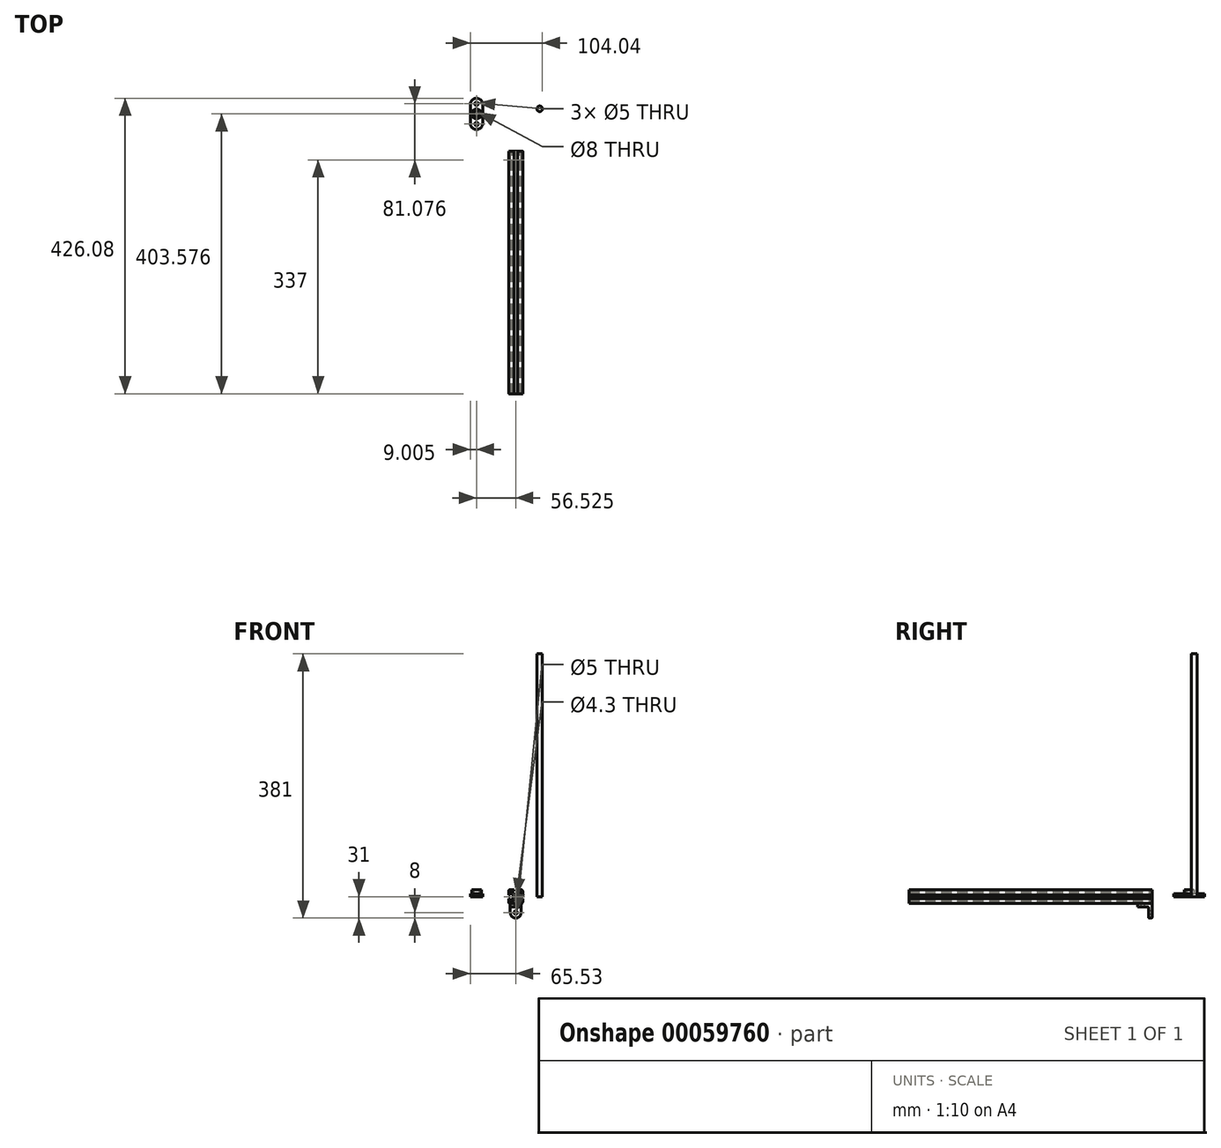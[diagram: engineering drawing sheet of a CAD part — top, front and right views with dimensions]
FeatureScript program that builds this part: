
annotation { "Feature Type Name" : "Feature", "Feature Type Description" : "" }
export const myFeature = defineFeature(function(context is Context, id is Id, definition is map)
    precondition{}
    {
        {
            var Q0;
            Q0=qCreatedBy(makeId("Front.planeOp"),FACE);
            var sketch = newSketch(context, id + "F0", { "sketchPlane" : qUnion([Q0])});
            skCircle(sketch, "E0", {"center": v(0, 0) * mm, "radius": 2.15 * mm});
            skLineSegment(sketch, "E1.bottom", {"start": v(-8, 10) * mm, "end": v(-2.5, 10) * mm});
            skLineSegment(sketch, "E1.top", {"start": v(-8, -10) * mm, "end": v(-2.5, -10) * mm});
            skLineSegment(sketch, "E1.left", {"start": v(-10, 8) * mm, "end": v(-10, 2.5) * mm});
            skLineSegment(sketch, "E1.right", {"start": v(10, 8) * mm, "end": v(10, 2.5) * mm});
            skLineSegment(sketch, "E2", {"start": v(-2.5, -19.05) * mm, "end": v(-2.5, -8.2) * mm, "construction": true});
            skLineSegment(sketch, "E3", {"start": v(-19.35, 2.5) * mm, "end": v(-8.2, 2.5) * mm, "construction": true});
            skLineSegment(sketch, "E4.MirrorCS", {"start": v(-19.35, -2.5) * mm, "end": v(-8.2, -2.5) * mm, "construction": true});
            skLineSegment(sketch, "E5.MirrorCS", {"start": v(2.5, -19.05) * mm, "end": v(2.5, -8.2) * mm, "construction": true});
            skPoint(sketch, "E6.visualSharp", {"position": v(-10, 10) * mm});
            skArc(sketch, "E6.filletArc", {"start": v(-8, 10) * mm, "mid": v(-9.41, 9.41) * mm, "end": v(-10, 8) * mm});
            skPoint(sketch, "E7.visualSharp", {"position": v(-10, -10) * mm});
            skArc(sketch, "E7.filletArc", {"start": v(-10, -8) * mm, "mid": v(-9.41, -9.41) * mm, "end": v(-8, -10) * mm});
            skPoint(sketch, "E8.visualSharp", {"position": v(10, 10) * mm});
            skArc(sketch, "E8.filletArc", {"start": v(10, 8) * mm, "mid": v(9.41, 9.41) * mm, "end": v(8, 10) * mm});
            skPoint(sketch, "E9.visualSharp", {"position": v(10, -10) * mm});
            skArc(sketch, "E9.filletArc", {"start": v(8, -10) * mm, "mid": v(9.41, -9.41) * mm, "end": v(10, -8) * mm});
            skLineSegment(sketch, "E10.bottom", {"start": v(-5.72, 8.2) * mm, "end": v(-2.5, 8.2) * mm, "construction": true});
            skLineSegment(sketch, "E10.top", {"start": v(-5.72, -8.2) * mm, "end": v(-2.5, -8.2) * mm});
            skLineSegment(sketch, "E10.left", {"start": v(-8.2, 5.84) * mm, "end": v(-8.2, 2.5) * mm});
            skLineSegment(sketch, "E10.right", {"start": v(8.2, 5.72) * mm, "end": v(8.2, 2.5) * mm});
            skLineSegment(sketch, "E11", {"start": v(-2.5, -8.2) * mm, "end": v(-2.5, -10) * mm});
            skLineSegment(sketch, "E12", {"start": v(2.5, -8.2) * mm, "end": v(2.5, -10) * mm});
            skLineSegment(sketch, "E13", {"start": v(-8.2, -2.5) * mm, "end": v(-10, -2.5) * mm});
            skLineSegment(sketch, "E14", {"start": v(-8.2, 2.5) * mm, "end": v(-10, 2.5) * mm});
            skLineSegment(sketch, "E15", {"start": v(8.2, 2.5) * mm, "end": v(10, 2.5) * mm});
            skLineSegment(sketch, "E16", {"start": v(-2.5, 8.2) * mm, "end": v(-2.5, 10) * mm});
            skLineSegment(sketch, "E17", {"start": v(2.5, 8.2) * mm, "end": v(2.5, 10) * mm});
            skLineSegment(sketch, "E18", {"start": v(-9.41, -9.41) * mm, "end": v(-1.52, -1.52) * mm, "construction": true});
            skLineSegment(sketch, "E19", {"start": v(-9.41, 9.41) * mm, "end": v(-2.5, 2.5) * mm, "construction": true});
            skLineSegment(sketch, "E20", {"start": v(-7.35, -6.07) * mm, "end": v(-3.65, -2.38) * mm});
            skLineSegment(sketch, "E21.MirrorCS", {"start": v(-6.07, -7.35) * mm, "end": v(-2.38, -3.65) * mm});
            skPoint(sketch, "E22.orphan", {"position": v(-11.42, 10.14) * mm});
            skPoint(sketch, "E23.orphan", {"position": v(-10.14, 11.42) * mm});
            skPoint(sketch, "E24.orphan", {"position": v(10.4, 11.68) * mm});
            skPoint(sketch, "E25.orphan", {"position": v(11.68, 10.4) * mm});
            skPoint(sketch, "E26.orphan", {"position": v(11.6, -10.32) * mm});
            skPoint(sketch, "E27.orphan", {"position": v(10.32, -11.6) * mm});
            skPoint(sketch, "E28.orphan", {"position": v(-13.16, -14.44) * mm});
            skPoint(sketch, "E29.orphan", {"position": v(-14.44, -13.16) * mm});
            skLineSegment(sketch, "E30.bottom", {"start": v(-2.38, 3.65) * mm, "end": v(2.38, 3.65) * mm});
            skLineSegment(sketch, "E30.top", {"start": v(-2.38, -3.65) * mm, "end": v(2.38, -3.65) * mm});
            skLineSegment(sketch, "E30.left", {"start": v(-3.65, 2.5) * mm, "end": v(-3.65, -2.38) * mm});
            skLineSegment(sketch, "E30.right", {"start": v(3.65, 2.38) * mm, "end": v(3.65, -2.38) * mm});
            skLineSegment(sketch, "E31.trimOffspring", {"start": v(2.38, -3.65) * mm, "end": v(6.07, -7.35) * mm});
            skLineSegment(sketch, "E32.trimOffspring", {"start": v(1.52, -1.52) * mm, "end": v(9.41, -9.41) * mm, "construction": true});
            skLineSegment(sketch, "E33.trimOffspring", {"start": v(3.65, -2.38) * mm, "end": v(7.35, -6.07) * mm});
            skLineSegment(sketch, "E34.trimOffspring", {"start": v(0, 0) * mm, "end": v(1.72, 1.72) * mm, "construction": true});
            skLineSegment(sketch, "E35.trimOffspring", {"start": v(1.52, 1.52) * mm, "end": v(9.41, 9.41) * mm, "construction": true});
            skLineSegment(sketch, "E36.trimOffspring", {"start": v(3.65, 2.38) * mm, "end": v(7.35, 6.07) * mm});
            skLineSegment(sketch, "E37.trimOffspring", {"start": v(8.2, 2.5) * mm, "end": v(18.34, 2.5) * mm, "construction": true});
            skLineSegment(sketch, "E38.trimOffspring", {"start": v(8.2, -2.5) * mm, "end": v(18.34, -2.5) * mm, "construction": true});
            skLineSegment(sketch, "E39.trimOffspring", {"start": v(-3.65, 2.5) * mm, "end": v(1.23, 2.5) * mm, "construction": true});
            skLineSegment(sketch, "E40.trimOffspring", {"start": v(-2.5, 8.2) * mm, "end": v(-2.5, 13.53) * mm, "construction": true});
            skLineSegment(sketch, "E41.trimOffspring", {"start": v(2.5, 8.2) * mm, "end": v(2.5, 13.53) * mm, "construction": true});
            skLineSegment(sketch, "E42", {"start": v(2.5, 8.2) * mm, "end": v(6.93, 8.2) * mm});
            skLineSegment(sketch, "E43", {"start": v(6.93, 8.2) * mm, "end": v(2.38, 3.65) * mm});
            skLineSegment(sketch, "E44", {"start": v(2.38, 3.65) * mm, "end": v(-2.38, 3.65) * mm});
            skLineSegment(sketch, "E45", {"start": v(-6.93, 8.2) * mm, "end": v(-2.5, 8.2) * mm});
            skLineSegment(sketch, "E46", {"start": v(-6.07, 7.35) * mm, "end": v(-2.38, 3.65) * mm});
            skLineSegment(sketch, "E47.trimOffspring", {"start": v(2.5, 8.2) * mm, "end": v(5.72, 8.2) * mm, "construction": true});
            skLineSegment(sketch, "E48.trimOffspring", {"start": v(8.2, -2.5) * mm, "end": v(8.2, -5.72) * mm});
            skLineSegment(sketch, "E49.trimOffspring", {"start": v(2.5, -8.2) * mm, "end": v(5.72, -8.2) * mm});
            skLineSegment(sketch, "E50.trimOffspring", {"start": v(-8.2, -2.5) * mm, "end": v(-8.2, -5.72) * mm});
            skPoint(sketch, "E51.orphan", {"position": v(3.65, 3.65) * mm});
            skPoint(sketch, "E52.orphan", {"position": v(3.65, -3.65) * mm});
            skPoint(sketch, "E53.orphan", {"position": v(-3.65, -3.65) * mm});
            skPoint(sketch, "E54.orphan", {"position": v(-3.65, 3.65) * mm});
            skLineSegment(sketch, "E55.trimOffspring", {"start": v(2.38, 3.65) * mm, "end": v(6.07, 7.35) * mm, "construction": true});
            skPoint(sketch, "E56.orphan", {"position": v(-8.2, 8.2) * mm});
            skPoint(sketch, "E57.orphan", {"position": v(8.2, 8.2) * mm});
            skPoint(sketch, "E58.orphan", {"position": v(8.2, -8.2) * mm});
            skPoint(sketch, "E59.orphan", {"position": v(-8.2, -8.2) * mm});
            skLineSegment(sketch, "E60.trimOffspring", {"start": v(2.5, 10) * mm, "end": v(8, 10) * mm});
            skLineSegment(sketch, "E61.trimOffspring", {"start": v(-10, -2.5) * mm, "end": v(-10, -8) * mm});
            skLineSegment(sketch, "E62.trimOffspring", {"start": v(2.5, -10) * mm, "end": v(8, -10) * mm});
            skLineSegment(sketch, "E63.trimOffspring", {"start": v(10, -2.5) * mm, "end": v(10, -8) * mm});
            skLineSegment(sketch, "E64", {"start": v(-7.35, 6.2) * mm, "end": v(-3.65, 2.5) * mm});
            skPoint(sketch, "E65.visualSharp", {"position": v(-8.2, 7.05) * mm});
            skArc(sketch, "E65.filletArc", {"start": v(-7.35, 6.2) * mm, "mid": v(-7.9, 6.3) * mm, "end": v(-8.2, 5.84) * mm});
            skPoint(sketch, "E66.visualSharp", {"position": v(-6.93, 8.2) * mm});
            skArc(sketch, "E66.filletArc", {"start": v(-5.72, 8.2) * mm, "mid": v(-6.18, 7.9) * mm, "end": v(-6.07, 7.35) * mm});
            skPoint(sketch, "E67.visualSharp", {"position": v(6.93, 8.2) * mm});
            skArc(sketch, "E67.filletArc", {"start": v(6.07, 7.35) * mm, "mid": v(6.18, 7.9) * mm, "end": v(5.72, 8.2) * mm, "construction": true});
            skPoint(sketch, "E68.visualSharp", {"position": v(8.2, 6.93) * mm});
            skArc(sketch, "E68.filletArc", {"start": v(8.2, 5.72) * mm, "mid": v(7.9, 6.18) * mm, "end": v(7.35, 6.07) * mm});
            skPoint(sketch, "E69.visualSharp", {"position": v(8.2, -6.93) * mm});
            skArc(sketch, "E69.filletArc", {"start": v(7.35, -6.07) * mm, "mid": v(7.9, -6.18) * mm, "end": v(8.2, -5.72) * mm});
            skPoint(sketch, "E70.visualSharp", {"position": v(6.93, -8.2) * mm});
            skArc(sketch, "E70.filletArc", {"start": v(5.72, -8.2) * mm, "mid": v(6.18, -7.9) * mm, "end": v(6.07, -7.35) * mm});
            skPoint(sketch, "E71.visualSharp", {"position": v(-6.93, -8.2) * mm});
            skArc(sketch, "E71.filletArc", {"start": v(-6.07, -7.35) * mm, "mid": v(-6.18, -7.9) * mm, "end": v(-5.72, -8.2) * mm});
            skPoint(sketch, "E72.visualSharp", {"position": v(-8.2, -6.93) * mm});
            skArc(sketch, "E72.filletArc", {"start": v(-8.2, -5.72) * mm, "mid": v(-7.9, -6.18) * mm, "end": v(-7.35, -6.07) * mm});
            skLineSegment(sketch, "E73", {"start": v(8.2, -2.5) * mm, "end": v(10, -2.5) * mm});
            skLineSegment(sketch, "E74", {"start": v(-5.21, 4.06) * mm, "end": v(-5.21, -3.94) * mm});
            skSolve(sketch);
        }
        {
            var Q0;
            Q0=makeQuery(id+"F0.imprint","IMPRINT",FACE,{"disambiguationData":[TD([[makeQuery(id+"F0.imprint","IMPRINT",EDGE,{"derivedFrom":sQuery(id+"F0.wireOp",EDGE,"E0")}),-1.0]])]});
            extrude(context, id + "F1", {"entities" : qUnion([Q0]), "depth" : 350 * mm});
        }
        {
            var Q0;
            Q0=makeQuery(id+"F1.opExtrude","SWEPT_FACE",FACE,{"disambiguationData":[OSD([sQuery(id+"F0.wireOp",EDGE,"E1.top")])]});
            var sketch = newSketch(context, id + "F2", { "sketchPlane" : qUnion([Q0])});
            skLineSegment(sketch, "E75.bottom", {"start": v(-7.8, 0) * mm, "end": v(7.8, 0) * mm});
            skLineSegment(sketch, "E75.top", {"start": v(-7.8, 21) * mm, "end": v(7.8, 21) * mm});
            skLineSegment(sketch, "E75.left", {"start": v(-7.8, 0) * mm, "end": v(-7.8, 21) * mm});
            skLineSegment(sketch, "E75.right", {"start": v(7.8, 0) * mm, "end": v(7.8, 21) * mm});
            skCircle(sketch, "E76", {"center": v(0, 13) * mm, "radius": 2.5 * mm});
            skPoint(sketch, "E76.centerSnap0", {"position": v(0, 21) * mm});
            skLineSegment(sketch, "E77.bottom", {"start": v(-4.8, 21) * mm, "end": v(4.8, 21) * mm});
            skLineSegment(sketch, "E77.top", {"start": v(-4.8, 5) * mm, "end": v(4.8, 5) * mm});
            skLineSegment(sketch, "E77.left", {"start": v(-4.8, 21) * mm, "end": v(-4.8, 5) * mm});
            skLineSegment(sketch, "E77.right", {"start": v(4.8, 21) * mm, "end": v(4.8, 5) * mm});
            skSolve(sketch);
        }
        {
            var Q0;
            Q0 = qSketchRegion(id + "F2", true);
            var Q1;
            Q1=makeQuery(id+"F2.imprint","IMPRINT",FACE,{"disambiguationData":[TD([[makeQuery(id+"F2.imprint","IMPRINT",EDGE,{"derivedFrom":sQuery(id+"F2.wireOp",EDGE,"E76")}),1.0]])]});
            extrude(context, id + "F3", {"entities" : qUnion([Q0, Q1]), "depth" : 21 * mm});
        }
        {
            var Q0;
            {var subQ4=sQuery(id+"F2.wireOp",EDGE,"E77.left");Q0=makeQuery(id+"F2.imprint","IMPRINT",FACE,{"disambiguationData":[TD([[makeQuery(id+"F2.imprint","IMPRINT",EDGE,{"derivedFrom":subQ4}),1.0]])]});}
            var Q1;
            {var subQ6=sQuery(id+"F2.wireOp",EDGE,"E76");Q1=makeQuery(id+"F2.imprint","IMPRINT",FACE,{"disambiguationData":[TD([[makeQuery(id+"F2.imprint","IMPRINT",EDGE,{"derivedFrom":subQ6}),-1.0]])]});}
            var Q2;
            Q2=makeQuery(id+"F2.imprint","IMPRINT",FACE,{"disambiguationData":[TD([[makeQuery(id+"F2.imprint","IMPRINT",EDGE,{"derivedFrom":sQuery(id+"F2.wireOp",EDGE,"E76")}),1.0]])]});
            extrude(context, id + "F4", {"entities" : qUnion([Q0, Q1, Q2]), "operationType" : NewBodyOperationType.REMOVE, "endBound" : BoundingType.THROUGH_ALL, "depth" : 3 * mm, "hasSecondDirection" : true, "secondDirectionOppositeDirection" : false, "secondDirectionDepth" : 5 * mm});
        }
        {
            var Q0;
            Q0=makeQuery(id+"F2.imprint","IMPRINT",FACE,{"disambiguationData":[TD([[makeQuery(id+"F2.imprint","IMPRINT",EDGE,{"derivedFrom":sQuery(id+"F2.wireOp",EDGE,"E76")}),1.0]])]});
            extrude(context, id + "F5", {"entities" : qUnion([Q0]), "operationType" : NewBodyOperationType.REMOVE, "endBound" : BoundingType.THROUGH_ALL, "depth" : 25 * mm});
        }
        {
            var Q0;
            Q0=makeQuery(id+"F4.boolean.opBoolean","COPY",FACE,{"derivedFrom":makeQuery(id+"F4.opExtrude","SWEPT_FACE",FACE,{"disambiguationData":[OSD([sQuery(id+"F2.wireOp",EDGE,"E77.top")])]})});
            var sketch = newSketch(context, id + "F6", { "sketchPlane" : qUnion([Q0])});
            skLineSegment(sketch, "E78.0.0", {"start": v(4.8, -31) * mm, "end": v(4.8, -15) * mm});
            skLineSegment(sketch, "E78.0.1", {"start": v(4.8, -15) * mm, "end": v(-4.8, -15) * mm});
            skLineSegment(sketch, "E78.0.2", {"start": v(-4.8, -15) * mm, "end": v(-4.8, -31) * mm});
            skLineSegment(sketch, "E78.0.3", {"start": v(-4.8, -31) * mm, "end": v(4.8, -31) * mm});
            skPoint(sketch, "E79.centerSnap0", {"position": v(-4.8, -23) * mm});
            skCircle(sketch, "E80", {"center": v(0, -23) * mm, "radius": 2.5 * mm});
            skSolve(sketch);
        }
        {
            var Q0;
            Q0=makeQuery(id+"F6.imprint","IMPRINT",FACE,{"disambiguationData":[TD([[makeQuery(id+"F6.imprint","IMPRINT",EDGE,{"derivedFrom":sQuery(id+"F6.wireOp",EDGE,"E79")}),1.0]])]});
            var Q1;
            Q1=makeQuery(id+"F6.imprint","IMPRINT",FACE,{"disambiguationData":[TD([[makeQuery(id+"F6.imprint","IMPRINT",EDGE,{"derivedFrom":sQuery(id+"F6.wireOp",EDGE,"E80")}),1.0]])]});
            extrude(context, id + "F7", {"entities" : qUnion([Q0, Q1]), "operationType" : NewBodyOperationType.REMOVE, "endBound" : BoundingType.THROUGH_ALL, "oppositeDirection" : true, "depth" : 25 * mm});
        }
        {
            var Q0;
            Q0=makeQuery(id+"F3.opExtrude","SWEPT_FACE",FACE,{"disambiguationData":[OSD([sQuery(id+"F2.wireOp",EDGE,"E75.right")])]});
            var sketch = newSketch(context, id + "F8", { "sketchPlane" : qUnion([Q0])});
            skLineSegment(sketch, "E81.0", {"start": v(-5, -31) * mm, "end": v(-5, -15) * mm});
            skLineSegment(sketch, "E82.0", {"start": v(-21, -15) * mm, "end": v(-5, -15) * mm});
            skSolve(sketch);
        }
        {
            var Q0;
            Q0=makeQuery(id+"F8.imprint","IMPRINT",FACE,{"disambiguationData":[TD([[makeQuery(id+"F8.imprint","IMPRINT",EDGE,{"derivedFrom":sQuery(id+"F8.wireOp",EDGE,"E81.0")}),1.0]])]});
            extrude(context, id + "F9", {"entities" : qUnion([Q0]), "operationType" : NewBodyOperationType.REMOVE, "oppositeDirection" : true, "depth" : 25 * mm});
        }
        {
            var Q0;
            Q0=makeQuery(id+"F3.opExtrude","SWEPT_EDGE",EDGE,{"disambiguationData":[OSD([sQuery(id+"F2.wireOp",EDGE,"E75.top"),sQuery(id+"F2.wireOp",EDGE,"E75.left")])]});
            var Q1;
            Q1=makeQuery(id+"F3.opExtrude","SWEPT_EDGE",EDGE,{"disambiguationData":[OSD([sQuery(id+"F2.wireOp",EDGE,"E75.top"),sQuery(id+"F2.wireOp",EDGE,"E75.right")])]});
            var Q2;
            Q2=makeQuery(id+"F3.opExtrude","CAP_EDGE",EDGE,{"disambiguationData":[OSD([sQuery(id+"F2.wireOp",EDGE,"E75.left")])],"isStart":false});
            var Q3;
            Q3=makeQuery(id+"F3.opExtrude","CAP_EDGE",EDGE,{"disambiguationData":[OSD([sQuery(id+"F2.wireOp",EDGE,"E75.right")])],"isStart":false});
            fillet(context, id + "F10", {"entities" : qUnion([Q0, Q1, Q2, Q3]), "radius" : 8 * mm, "tangentPropagation" : true, "allowEdgeOverflow" : false});
        }
        {
            var Q0;
            Q0=makeQuery(id+"F3.opExtrude","CAP_EDGE",EDGE,{"disambiguationData":[OSD([sQuery(id+"F2.wireOp",EDGE,"E75.bottom")])],"isStart":true});
            var Q1;
            Q1=makeQuery(id+"F4.boolean.opBoolean","COPY",EDGE,{"derivedFrom":makeQuery(id+"F4.opExtrude","CAP_EDGE",EDGE,{"disambiguationData":[OSD([sQuery(id+"F2.wireOp",EDGE,"E77.top")])],"isStart":true})});
            var Q2;
            Q2=makeQuery(id+"F3.opExtrude","SWEPT_EDGE",EDGE,{"disambiguationData":[OSD([sQuery(id+"F0.wireOp",EDGE,"E1.top"),sQuery(id+"F2.wireOp",EDGE,"E75.bottom"),sQuery(id+"F2.wireOp",EDGE,"E75.left")])]});
            var Q3;
            Q3=makeQuery(id+"F10.opFillet","BLEND_EDGE",EDGE,{"blendedFrom":[makeQuery(id+"F3.opExtrude","CAP_EDGE",EDGE,{"disambiguationData":[OSD([sQuery(id+"F2.wireOp",EDGE,"E75.left")])],"isStart":false}),makeQuery(id+"F3.opExtrude","SWEPT_FACE",FACE,{"disambiguationData":[OSD([sQuery(id+"F2.wireOp",EDGE,"E75.bottom")])]})],"blendedInto":[makeQuery(id+"F3.opExtrude","SWEPT_FACE",FACE,{"disambiguationData":[OSD([sQuery(id+"F2.wireOp",EDGE,"E75.bottom")])]})]});
            var Q4;
            Q4=makeQuery(id+"F10.opFillet","BLEND_EDGE",EDGE,{"blendedFrom":[makeQuery(id+"F3.opExtrude","CAP_EDGE",EDGE,{"disambiguationData":[OSD([sQuery(id+"F2.wireOp",EDGE,"E75.right")])],"isStart":false}),makeQuery(id+"F3.opExtrude","SWEPT_FACE",FACE,{"disambiguationData":[OSD([sQuery(id+"F2.wireOp",EDGE,"E75.bottom")])]})],"blendedInto":[makeQuery(id+"F3.opExtrude","SWEPT_FACE",FACE,{"disambiguationData":[OSD([sQuery(id+"F2.wireOp",EDGE,"E75.bottom")])]})]});
            var Q5;
            Q5=makeQuery(id+"F3.opExtrude","SWEPT_EDGE",EDGE,{"disambiguationData":[OSD([sQuery(id+"F2.wireOp",EDGE,"E75.bottom"),sQuery(id+"F2.wireOp",EDGE,"E75.right")])]});
            var Q6;
            Q6=makeQuery(id+"F3.opExtrude","CAP_EDGE",EDGE,{"disambiguationData":[OSD([sQuery(id+"F2.wireOp",EDGE,"E75.left")])],"isStart":true});
            var Q7;
            {var subQ0=sQuery(id+"F2.wireOp",EDGE,"E75.left");var subQ1=sQuery(id+"F2.wireOp",EDGE,"E75.top");Q7=makeQuery(id+"F10.opFillet","BLEND_EDGE",EDGE,{"blendedFrom":[makeQuery(id+"F3.opExtrude","SWEPT_EDGE",EDGE,{"disambiguationData":[OSD([subQ1,subQ0])]}),makeQuery(id+"F3.opExtrude","CAP_FACE",FACE,{"disambiguationData":[OSD([sQuery(id+"F2.wireOp",EDGE,"E75.bottom"),subQ1,subQ0,sQuery(id+"F2.wireOp",EDGE,"E75.right"),sQuery(id+"F2.wireOp",EDGE,"E77.bottom"),sQuery(id+"F2.wireOp",EDGE,"m4iLFzGu-l6cL-oS4W-GvPt-0jt0GClDsFra")])],"isStart":true})],"blendedInto":[makeQuery(id+"F3.opExtrude","CAP_FACE",FACE,{"disambiguationData":[OSD([sQuery(id+"F2.wireOp",EDGE,"E75.bottom"),subQ1,subQ0,sQuery(id+"F2.wireOp",EDGE,"E75.right"),sQuery(id+"F2.wireOp",EDGE,"E77.bottom"),sQuery(id+"F2.wireOp",EDGE,"m4iLFzGu-l6cL-oS4W-GvPt-0jt0GClDsFra")])],"isStart":true})]});}
            var Q8;
            {var subQ0=sQuery(id+"F2.wireOp",EDGE,"E75.right");var subQ1=sQuery(id+"F2.wireOp",EDGE,"E75.top");Q8=makeQuery(id+"F10.opFillet","BLEND_EDGE",EDGE,{"blendedFrom":[makeQuery(id+"F3.opExtrude","SWEPT_EDGE",EDGE,{"disambiguationData":[OSD([subQ1,subQ0])]}),makeQuery(id+"F3.opExtrude","CAP_FACE",FACE,{"disambiguationData":[OSD([sQuery(id+"F2.wireOp",EDGE,"E75.bottom"),subQ1,sQuery(id+"F2.wireOp",EDGE,"E75.left"),subQ0,sQuery(id+"F2.wireOp",EDGE,"E77.bottom"),sQuery(id+"F2.wireOp",EDGE,"m4iLFzGu-l6cL-oS4W-GvPt-0jt0GClDsFra")])],"isStart":true})],"blendedInto":[makeQuery(id+"F3.opExtrude","CAP_FACE",FACE,{"disambiguationData":[OSD([sQuery(id+"F2.wireOp",EDGE,"E75.bottom"),subQ1,sQuery(id+"F2.wireOp",EDGE,"E75.left"),subQ0,sQuery(id+"F2.wireOp",EDGE,"E77.bottom"),sQuery(id+"F2.wireOp",EDGE,"m4iLFzGu-l6cL-oS4W-GvPt-0jt0GClDsFra")])],"isStart":true})]});}
            var Q9;
            Q9=makeQuery(id+"F3.opExtrude","CAP_EDGE",EDGE,{"disambiguationData":[OSD([sQuery(id+"F2.wireOp",EDGE,"E75.right")])],"isStart":true});
            var Q10;
            Q10=makeQuery(id+"F9.boolean.opBoolean","INTERSECT",EDGE,{"derivedFrom":[makeQuery(id+"F3.opExtrude","SWEPT_FACE",FACE,{"disambiguationData":[OSD([sQuery(id+"F2.wireOp",EDGE,"E75.left")])]}),makeQuery(id+"F9.opExtrude","SWEPT_FACE",FACE,{"disambiguationData":[OSD([sQuery(id+"F8.wireOp",EDGE,"E81.0")])]})]});
            var Q11;
            Q11=makeQuery(id+"F10.opFillet","BLEND_EDGE",EDGE,{"blendedFrom":[makeQuery(id+"F3.opExtrude","CAP_EDGE",EDGE,{"disambiguationData":[OSD([sQuery(id+"F2.wireOp",EDGE,"E75.left")])],"isStart":false}),makeQuery(id+"F9.boolean.opBoolean","MERGE",FACE,{"derivedFrom":[makeQuery(id+"F4.boolean.opBoolean","COPY",FACE,{"derivedFrom":makeQuery(id+"F4.opExtrude","SWEPT_FACE",FACE,{"disambiguationData":[OSD([sQuery(id+"F2.wireOp",EDGE,"E77.top")])]})}),makeQuery(id+"F9.opExtrude","SWEPT_FACE",FACE,{"disambiguationData":[OSD([sQuery(id+"F8.wireOp",EDGE,"E81.0")])]})]})],"blendedInto":[makeQuery(id+"F9.boolean.opBoolean","MERGE",FACE,{"derivedFrom":[makeQuery(id+"F4.boolean.opBoolean","COPY",FACE,{"derivedFrom":makeQuery(id+"F4.opExtrude","SWEPT_FACE",FACE,{"disambiguationData":[OSD([sQuery(id+"F2.wireOp",EDGE,"E77.top")])]})}),makeQuery(id+"F9.opExtrude","SWEPT_FACE",FACE,{"disambiguationData":[OSD([sQuery(id+"F8.wireOp",EDGE,"E81.0")])]})]})]});
            var Q12;
            Q12=makeQuery(id+"F10.opFillet","BLEND_EDGE",EDGE,{"blendedFrom":[makeQuery(id+"F3.opExtrude","CAP_EDGE",EDGE,{"disambiguationData":[OSD([sQuery(id+"F2.wireOp",EDGE,"E75.right")])],"isStart":false}),makeQuery(id+"F9.boolean.opBoolean","MERGE",FACE,{"derivedFrom":[makeQuery(id+"F4.boolean.opBoolean","COPY",FACE,{"derivedFrom":makeQuery(id+"F4.opExtrude","SWEPT_FACE",FACE,{"disambiguationData":[OSD([sQuery(id+"F2.wireOp",EDGE,"E77.top")])]})}),makeQuery(id+"F9.opExtrude","SWEPT_FACE",FACE,{"disambiguationData":[OSD([sQuery(id+"F8.wireOp",EDGE,"E81.0")])]})]})],"blendedInto":[makeQuery(id+"F9.boolean.opBoolean","MERGE",FACE,{"derivedFrom":[makeQuery(id+"F4.boolean.opBoolean","COPY",FACE,{"derivedFrom":makeQuery(id+"F4.opExtrude","SWEPT_FACE",FACE,{"disambiguationData":[OSD([sQuery(id+"F2.wireOp",EDGE,"E77.top")])]})}),makeQuery(id+"F9.opExtrude","SWEPT_FACE",FACE,{"disambiguationData":[OSD([sQuery(id+"F8.wireOp",EDGE,"E81.0")])]})]})]});
            fillet(context, id + "F11", {"entities" : qUnion([Q0, Q1, Q2, Q3, Q4, Q5, Q6, Q7, Q8, Q9, Q10, Q11, Q12]), "radius" : 1 * mm, "tangentPropagation" : true, "allowEdgeOverflow" : false});
        }
        {
            var Q0;
            Q0=qCreatedBy(makeId("Top.planeOp"),FACE);
            var sketch = newSketch(context, id + "F12", { "sketchPlane" : qUnion([Q0])});
            skCircle(sketch, "E83", {"center": v(34.51, 60.98) * mm, "radius": 4 * mm});
            skSolve(sketch);
        }
        {
            var Q0;
            Q0=makeQuery(id+"F12.imprint","IMPRINT",FACE,{"disambiguationData":[TD([[makeQuery(id+"F12.imprint","IMPRINT",EDGE,{"derivedFrom":sQuery(id+"F12.wireOp",EDGE,"E83")}),1.0]])]});
            extrude(context, id + "F13", {"entities" : qUnion([Q0]), "depth" : 350 * mm});
        }
        {
            var Q0;
            Q0=qCreatedBy(makeId("Top.planeOp"),FACE);
            var sketch = newSketch(context, id + "F14", { "sketchPlane" : qUnion([Q0])});
            skCircle(sketch, "E84", {"center": v(-56.53, 53.58) * mm, "radius": 4 * mm});
            skCircle(sketch, "E85", {"center": v(-56.53, 53.58) * mm, "radius": 7 * mm});
            skLineSegment(sketch, "E86.bottom", {"start": v(-56.53, 76.08) * mm, "end": v(-56.53, 76.08) * mm});
            skLineSegment(sketch, "E86.top", {"start": v(-56.53, 31.08) * mm, "end": v(-56.53, 31.08) * mm});
            skLineSegment(sketch, "E86.left", {"start": v(-65.53, 67.08) * mm, "end": v(-65.53, 40.08) * mm});
            skLineSegment(sketch, "E86.right", {"start": v(-47.53, 67.08) * mm, "end": v(-47.53, 40.08) * mm});
            skCircle(sketch, "E87", {"center": v(-56.53, 39.08) * mm, "radius": 2.5 * mm});
            skCircle(sketch, "E88", {"center": v(-56.53, 68.08) * mm, "radius": 2.5 * mm});
            skPoint(sketch, "E89.visualSharp", {"position": v(-65.53, 76.08) * mm});
            skArc(sketch, "E89.filletArc", {"start": v(-56.53, 76.08) * mm, "mid": v(-62.89, 73.44) * mm, "end": v(-65.53, 67.08) * mm});
            skPoint(sketch, "E90.visualSharp", {"position": v(-47.53, 76.08) * mm});
            skArc(sketch, "E90.filletArc", {"start": v(-47.53, 67.08) * mm, "mid": v(-50.16, 73.44) * mm, "end": v(-56.53, 76.08) * mm});
            skPoint(sketch, "E91.visualSharp", {"position": v(-65.53, 31.08) * mm});
            skArc(sketch, "E91.filletArc", {"start": v(-65.53, 40.08) * mm, "mid": v(-62.89, 33.71) * mm, "end": v(-56.53, 31.08) * mm});
            skPoint(sketch, "E92.visualSharp", {"position": v(-47.53, 31.08) * mm});
            skArc(sketch, "E92.filletArc", {"start": v(-56.53, 31.08) * mm, "mid": v(-50.16, 33.71) * mm, "end": v(-47.53, 40.08) * mm});
            skSolve(sketch);
        }
        {
            var Q0;
            Q0=makeQuery(id+"F14.imprint","IMPRINT",FACE,{"disambiguationData":[TD([[makeQuery(id+"F14.imprint","IMPRINT",EDGE,{"derivedFrom":sQuery(id+"F14.wireOp",EDGE,"E85")}),-1.0]])]});
            extrude(context, id + "F15", {"entities" : qUnion([Q0]), "depth" : 4 * mm});
        }
        {
            var Q0;
            Q0=makeQuery(id+"F14.imprint","IMPRINT",FACE,{"disambiguationData":[TD([[makeQuery(id+"F14.imprint","IMPRINT",EDGE,{"derivedFrom":sQuery(id+"F14.wireOp",EDGE,"E84")}),-1.0]])]});
            extrude(context, id + "F16", {"entities" : qUnion([Q0]), "operationType" : NewBodyOperationType.ADD, "depth" : 10 * mm});
        }
    });
